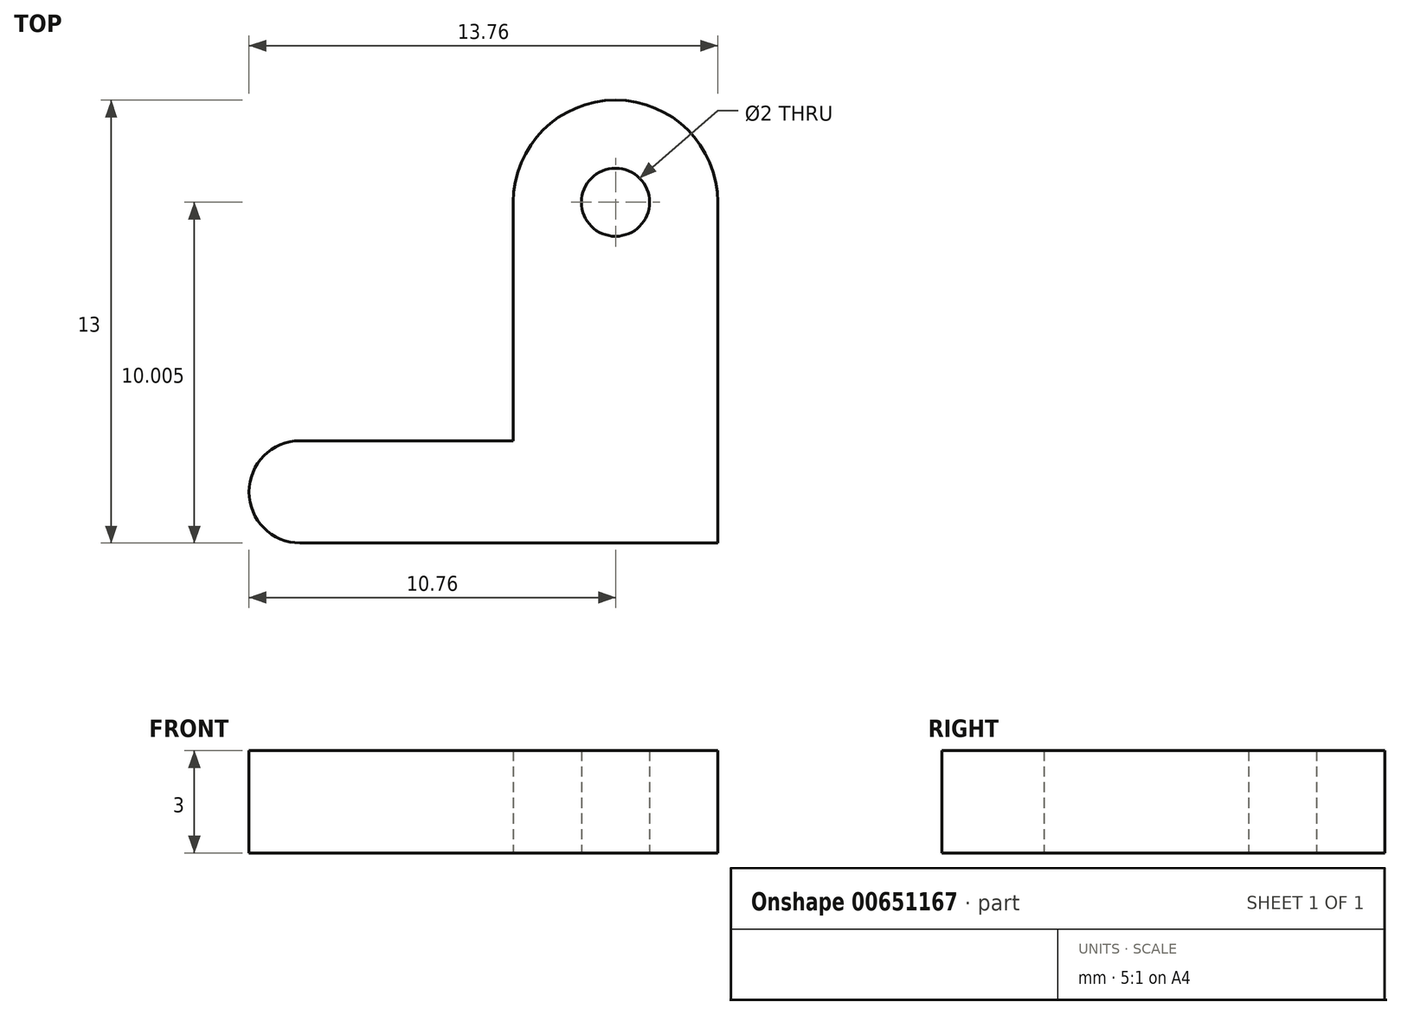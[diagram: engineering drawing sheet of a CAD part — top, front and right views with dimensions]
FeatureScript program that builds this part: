
annotation { "Feature Type Name" : "Feature", "Feature Type Description" : "" }
export const myFeature = defineFeature(function(context is Context, id is Id, definition is map)
    precondition{}
    {
        {
            var Q0;
            Q0=qCreatedBy(makeId("Top.planeOp"),FACE);
            var sketch = newSketch(context, id + "F0", { "sketchPlane" : qUnion([Q0])});
            skLineSegment(sketch, "E0", {"start": v(-12.26, 3) * mm, "end": v(-6, 3) * mm});
            skLineSegment(sketch, "E1", {"start": v(-6, 3) * mm, "end": v(-6, 10) * mm});
            skLineSegment(sketch, "E2", {"start": v(-12.26, 0) * mm, "end": v(0, 0) * mm});
            skLineSegment(sketch, "E3", {"start": v(0, 0) * mm, "end": v(0, 10) * mm});
            skArc(sketch, "E4", {"start": v(0, 10) * mm, "mid": v(-3, 13) * mm, "end": v(-6, 10) * mm});
            skArc(sketch, "E5", {"start": v(-12.26, 3) * mm, "mid": v(-13.76, 1.5) * mm, "end": v(-12.26, 0) * mm});
            skCircle(sketch, "E6", {"center": v(-3, 10) * mm, "radius": 1 * mm});
            skSolve(sketch);
        }
        {
            var Q0;
            Q0=makeQuery(id+"F0.imprint","IMPRINT",FACE,{"disambiguationData":[TD([[makeQuery(id+"F0.imprint","IMPRINT",EDGE,{"derivedFrom":sQuery(id+"F0.wireOp",EDGE,"E0")}),-1.0]])]});
            extrude(context, id + "F1", {"entities" : qUnion([Q0]), "depth" : 3 * mm, "offsetDistance" : 25 * mm});
        }
    });
